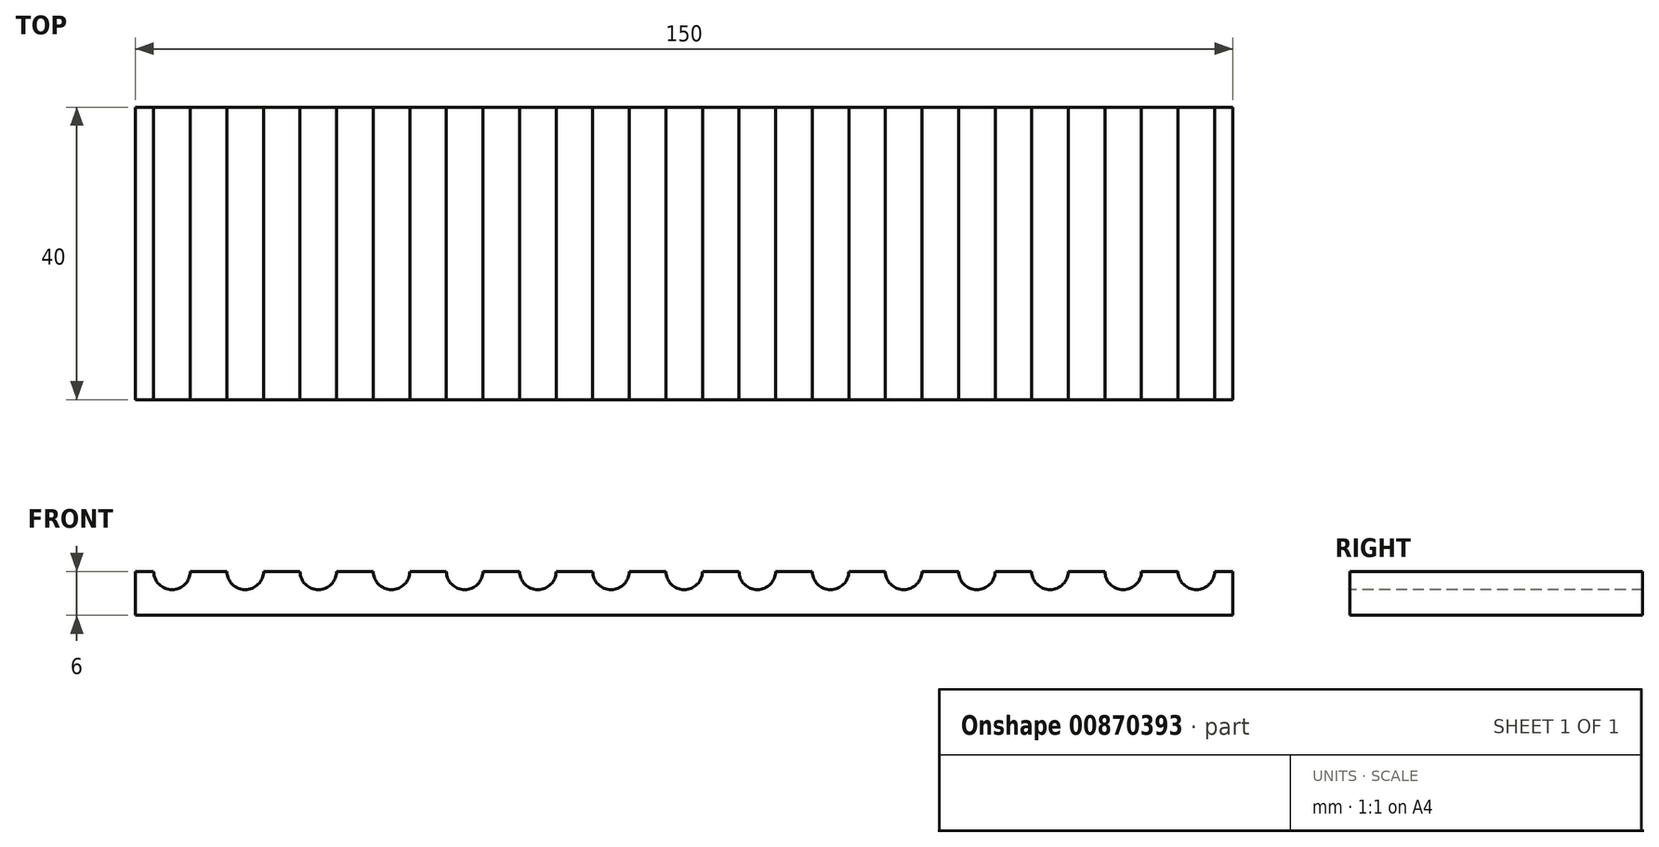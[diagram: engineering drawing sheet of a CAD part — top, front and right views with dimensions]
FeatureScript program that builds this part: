
annotation { "Feature Type Name" : "Feature", "Feature Type Description" : "" }
export const myFeature = defineFeature(function(context is Context, id is Id, definition is map)
    precondition{}
    {
        {
            var Q0;
            Q0=qCreatedBy(makeId("Front.planeOp"),FACE);
            var sketch = newSketch(context, id + "F0", { "sketchPlane" : qUnion([Q0])});
            skLineSegment(sketch, "E0.bottom", {"start": v(0, 0) * mm, "end": v(150, 0) * mm});
            skLineSegment(sketch, "E0.top", {"start": v(0, 6) * mm, "end": v(150, 6) * mm});
            skLineSegment(sketch, "E0.left", {"start": v(0, 0) * mm, "end": v(0, 6) * mm});
            skLineSegment(sketch, "E0.right", {"start": v(150, 0) * mm, "end": v(150, 6) * mm});
            skSolve(sketch);
        }
        {
            var Q0;
            Q0=makeQuery(id+"F0.imprint","IMPRINT",FACE,{"disambiguationData":[TD([[makeQuery(id+"F0.imprint","IMPRINT",EDGE,{"derivedFrom":sQuery(id+"F0.wireOp",EDGE,"E0.bottom")}),1.0]])]});
            extrude(context, id + "F1", {"entities" : qUnion([Q0]), "oppositeDirection" : true, "depth" : 40 * mm, "offsetDistance" : 25 * mm});
        }
        {
            var Q0;
            Q0=makeQuery(id+"F1.opExtrude","CAP_FACE",FACE,{"disambiguationData":[OSD([sQuery(id+"F0.wireOp",EDGE,"E0.bottom"),sQuery(id+"F0.wireOp",EDGE,"E0.top"),sQuery(id+"F0.wireOp",EDGE,"E0.left"),sQuery(id+"F0.wireOp",EDGE,"E0.right")])],"isStart":true});
            var sketch = newSketch(context, id + "F2", { "sketchPlane" : qUnion([Q0])});
            skCircle(sketch, "E1", {"center": v(5, 6) * mm, "radius": 2.5 * mm});
            skCircle(sketch, "E2.1.0.0", {"center": v(15, 6) * mm, "radius": 2.5 * mm});
            skCircle(sketch, "E2.2.0.0", {"center": v(25, 6) * mm, "radius": 2.5 * mm});
            skCircle(sketch, "E2.3.0.0", {"center": v(35, 6) * mm, "radius": 2.5 * mm});
            skCircle(sketch, "E2.4.0.0", {"center": v(45, 6) * mm, "radius": 2.5 * mm});
            skCircle(sketch, "E2.5.0.0", {"center": v(55, 6) * mm, "radius": 2.5 * mm});
            skCircle(sketch, "E2.6.0.0", {"center": v(65, 6) * mm, "radius": 2.5 * mm});
            skCircle(sketch, "E2.7.0.0", {"center": v(75, 6) * mm, "radius": 2.5 * mm});
            skCircle(sketch, "E2.8.0.0", {"center": v(85, 6) * mm, "radius": 2.5 * mm});
            skCircle(sketch, "E2.9.0.0", {"center": v(95, 6) * mm, "radius": 2.5 * mm});
            skCircle(sketch, "E2.10.0.0", {"center": v(105, 6) * mm, "radius": 2.5 * mm});
            skCircle(sketch, "E2.11.0.0", {"center": v(115, 6) * mm, "radius": 2.5 * mm});
            skCircle(sketch, "E2.12.0.0", {"center": v(125, 6) * mm, "radius": 2.5 * mm});
            skCircle(sketch, "E2.13.0.0", {"center": v(135, 6) * mm, "radius": 2.5 * mm});
            skCircle(sketch, "E2.14.0.0", {"center": v(145, 6) * mm, "radius": 2.5 * mm});
            skLineSegment(sketch, "E2.direction1", {"start": v(5, 6) * mm, "end": v(15, 6) * mm, "construction": true});
            skSolve(sketch);
        }
        {
            var Q0;
            {var subQ0=sQuery(id+"F2.wireOp",EDGE,"E1");var subQ1=makeQuery(id+"F1.opExtrude","CAP_EDGE",EDGE,{"disambiguationData":[OSD([sQuery(id+"F0.wireOp",EDGE,"E0.top")])],"isStart":true});var subQ2=makeQuery(id+"F2.imprint","INTERSECT",VERTEX,{"disambiguationData":[OD(0.0)],"derivedFrom":[subQ1,subQ0]});Q0=makeQuery(id+"F2.imprint","IMPRINT",FACE,{"disambiguationData":[TD([[makeQuery(id+"F2.imprint","IMPRINT",EDGE,{"disambiguationData":[TD([[subQ2,-1.0]])],"derivedFrom":subQ0}),1.0]])]});}
            var Q1;
            {var subQ0=sQuery(id+"F2.wireOp",EDGE,"E2.1.0.0");var subQ1=makeQuery(id+"F1.opExtrude","CAP_EDGE",EDGE,{"disambiguationData":[OSD([sQuery(id+"F0.wireOp",EDGE,"E0.top")])],"isStart":true});var subQ2=makeQuery(id+"F2.imprint","INTERSECT",VERTEX,{"disambiguationData":[OD(0.0)],"derivedFrom":[subQ1,subQ0]});Q1=makeQuery(id+"F2.imprint","IMPRINT",FACE,{"disambiguationData":[TD([[makeQuery(id+"F2.imprint","IMPRINT",EDGE,{"disambiguationData":[TD([[subQ2,-1.0]])],"derivedFrom":subQ0}),1.0]])]});}
            var Q2;
            {var subQ0=sQuery(id+"F2.wireOp",EDGE,"E2.2.0.0");var subQ1=makeQuery(id+"F1.opExtrude","CAP_EDGE",EDGE,{"disambiguationData":[OSD([sQuery(id+"F0.wireOp",EDGE,"E0.top")])],"isStart":true});var subQ2=makeQuery(id+"F2.imprint","INTERSECT",VERTEX,{"disambiguationData":[OD(0.0)],"derivedFrom":[subQ1,subQ0]});Q2=makeQuery(id+"F2.imprint","IMPRINT",FACE,{"disambiguationData":[TD([[makeQuery(id+"F2.imprint","IMPRINT",EDGE,{"disambiguationData":[TD([[subQ2,-1.0]])],"derivedFrom":subQ0}),1.0]])]});}
            var Q3;
            {var subQ0=sQuery(id+"F2.wireOp",EDGE,"E2.3.0.0");var subQ1=makeQuery(id+"F1.opExtrude","CAP_EDGE",EDGE,{"disambiguationData":[OSD([sQuery(id+"F0.wireOp",EDGE,"E0.top")])],"isStart":true});var subQ2=makeQuery(id+"F2.imprint","INTERSECT",VERTEX,{"disambiguationData":[OD(0.0)],"derivedFrom":[subQ1,subQ0]});Q3=makeQuery(id+"F2.imprint","IMPRINT",FACE,{"disambiguationData":[TD([[makeQuery(id+"F2.imprint","IMPRINT",EDGE,{"disambiguationData":[TD([[subQ2,-1.0]])],"derivedFrom":subQ0}),1.0]])]});}
            var Q4;
            {var subQ0=sQuery(id+"F2.wireOp",EDGE,"E2.4.0.0");var subQ1=makeQuery(id+"F1.opExtrude","CAP_EDGE",EDGE,{"disambiguationData":[OSD([sQuery(id+"F0.wireOp",EDGE,"E0.top")])],"isStart":true});var subQ2=makeQuery(id+"F2.imprint","INTERSECT",VERTEX,{"disambiguationData":[OD(0.0)],"derivedFrom":[subQ1,subQ0]});Q4=makeQuery(id+"F2.imprint","IMPRINT",FACE,{"disambiguationData":[TD([[makeQuery(id+"F2.imprint","IMPRINT",EDGE,{"disambiguationData":[TD([[subQ2,-1.0]])],"derivedFrom":subQ0}),1.0]])]});}
            var Q5;
            {var subQ0=sQuery(id+"F2.wireOp",EDGE,"E2.5.0.0");var subQ1=makeQuery(id+"F1.opExtrude","CAP_EDGE",EDGE,{"disambiguationData":[OSD([sQuery(id+"F0.wireOp",EDGE,"E0.top")])],"isStart":true});var subQ2=makeQuery(id+"F2.imprint","INTERSECT",VERTEX,{"disambiguationData":[OD(0.0)],"derivedFrom":[subQ1,subQ0]});Q5=makeQuery(id+"F2.imprint","IMPRINT",FACE,{"disambiguationData":[TD([[makeQuery(id+"F2.imprint","IMPRINT",EDGE,{"disambiguationData":[TD([[subQ2,-1.0]])],"derivedFrom":subQ0}),1.0]])]});}
            var Q6;
            {var subQ0=sQuery(id+"F2.wireOp",EDGE,"E2.6.0.0");var subQ1=makeQuery(id+"F1.opExtrude","CAP_EDGE",EDGE,{"disambiguationData":[OSD([sQuery(id+"F0.wireOp",EDGE,"E0.top")])],"isStart":true});var subQ2=makeQuery(id+"F2.imprint","INTERSECT",VERTEX,{"disambiguationData":[OD(0.0)],"derivedFrom":[subQ1,subQ0]});Q6=makeQuery(id+"F2.imprint","IMPRINT",FACE,{"disambiguationData":[TD([[makeQuery(id+"F2.imprint","IMPRINT",EDGE,{"disambiguationData":[TD([[subQ2,-1.0]])],"derivedFrom":subQ0}),1.0]])]});}
            var Q7;
            {var subQ0=sQuery(id+"F2.wireOp",EDGE,"E2.7.0.0");var subQ1=makeQuery(id+"F1.opExtrude","CAP_EDGE",EDGE,{"disambiguationData":[OSD([sQuery(id+"F0.wireOp",EDGE,"E0.top")])],"isStart":true});var subQ2=makeQuery(id+"F2.imprint","INTERSECT",VERTEX,{"disambiguationData":[OD(0.0)],"derivedFrom":[subQ1,subQ0]});Q7=makeQuery(id+"F2.imprint","IMPRINT",FACE,{"disambiguationData":[TD([[makeQuery(id+"F2.imprint","IMPRINT",EDGE,{"disambiguationData":[TD([[subQ2,-1.0]])],"derivedFrom":subQ0}),1.0]])]});}
            var Q8;
            {var subQ0=sQuery(id+"F2.wireOp",EDGE,"E2.8.0.0");var subQ1=makeQuery(id+"F1.opExtrude","CAP_EDGE",EDGE,{"disambiguationData":[OSD([sQuery(id+"F0.wireOp",EDGE,"E0.top")])],"isStart":true});var subQ2=makeQuery(id+"F2.imprint","INTERSECT",VERTEX,{"disambiguationData":[OD(0.0)],"derivedFrom":[subQ1,subQ0]});Q8=makeQuery(id+"F2.imprint","IMPRINT",FACE,{"disambiguationData":[TD([[makeQuery(id+"F2.imprint","IMPRINT",EDGE,{"disambiguationData":[TD([[subQ2,1.0]])],"derivedFrom":subQ0}),1.0]])]});}
            var Q9;
            {var subQ0=sQuery(id+"F2.wireOp",EDGE,"E2.9.0.0");var subQ1=makeQuery(id+"F1.opExtrude","CAP_EDGE",EDGE,{"disambiguationData":[OSD([sQuery(id+"F0.wireOp",EDGE,"E0.top")])],"isStart":true});var subQ2=makeQuery(id+"F2.imprint","INTERSECT",VERTEX,{"disambiguationData":[OD(0.0)],"derivedFrom":[subQ1,subQ0]});Q9=makeQuery(id+"F2.imprint","IMPRINT",FACE,{"disambiguationData":[TD([[makeQuery(id+"F2.imprint","IMPRINT",EDGE,{"disambiguationData":[TD([[subQ2,1.0]])],"derivedFrom":subQ0}),1.0]])]});}
            var Q10;
            {var subQ0=sQuery(id+"F2.wireOp",EDGE,"E2.10.0.0");var subQ1=makeQuery(id+"F1.opExtrude","CAP_EDGE",EDGE,{"disambiguationData":[OSD([sQuery(id+"F0.wireOp",EDGE,"E0.top")])],"isStart":true});var subQ2=makeQuery(id+"F2.imprint","INTERSECT",VERTEX,{"disambiguationData":[OD(0.0)],"derivedFrom":[subQ1,subQ0]});Q10=makeQuery(id+"F2.imprint","IMPRINT",FACE,{"disambiguationData":[TD([[makeQuery(id+"F2.imprint","IMPRINT",EDGE,{"disambiguationData":[TD([[subQ2,1.0]])],"derivedFrom":subQ0}),1.0]])]});}
            var Q11;
            {var subQ0=sQuery(id+"F2.wireOp",EDGE,"E2.11.0.0");var subQ1=makeQuery(id+"F1.opExtrude","CAP_EDGE",EDGE,{"disambiguationData":[OSD([sQuery(id+"F0.wireOp",EDGE,"E0.top")])],"isStart":true});var subQ2=makeQuery(id+"F2.imprint","INTERSECT",VERTEX,{"disambiguationData":[OD(0.0)],"derivedFrom":[subQ1,subQ0]});Q11=makeQuery(id+"F2.imprint","IMPRINT",FACE,{"disambiguationData":[TD([[makeQuery(id+"F2.imprint","IMPRINT",EDGE,{"disambiguationData":[TD([[subQ2,1.0]])],"derivedFrom":subQ0}),1.0]])]});}
            var Q12;
            {var subQ0=sQuery(id+"F2.wireOp",EDGE,"E2.12.0.0");var subQ1=makeQuery(id+"F1.opExtrude","CAP_EDGE",EDGE,{"disambiguationData":[OSD([sQuery(id+"F0.wireOp",EDGE,"E0.top")])],"isStart":true});var subQ2=makeQuery(id+"F2.imprint","INTERSECT",VERTEX,{"disambiguationData":[OD(0.0)],"derivedFrom":[subQ1,subQ0]});Q12=makeQuery(id+"F2.imprint","IMPRINT",FACE,{"disambiguationData":[TD([[makeQuery(id+"F2.imprint","IMPRINT",EDGE,{"disambiguationData":[TD([[subQ2,1.0]])],"derivedFrom":subQ0}),1.0]])]});}
            var Q13;
            {var subQ0=sQuery(id+"F2.wireOp",EDGE,"E2.13.0.0");var subQ1=makeQuery(id+"F1.opExtrude","CAP_EDGE",EDGE,{"disambiguationData":[OSD([sQuery(id+"F0.wireOp",EDGE,"E0.top")])],"isStart":true});var subQ2=makeQuery(id+"F2.imprint","INTERSECT",VERTEX,{"disambiguationData":[OD(0.0)],"derivedFrom":[subQ1,subQ0]});Q13=makeQuery(id+"F2.imprint","IMPRINT",FACE,{"disambiguationData":[TD([[makeQuery(id+"F2.imprint","IMPRINT",EDGE,{"disambiguationData":[TD([[subQ2,1.0]])],"derivedFrom":subQ0}),1.0]])]});}
            var Q14;
            {var subQ0=sQuery(id+"F2.wireOp",EDGE,"E2.14.0.0");var subQ1=makeQuery(id+"F1.opExtrude","CAP_EDGE",EDGE,{"disambiguationData":[OSD([sQuery(id+"F0.wireOp",EDGE,"E0.top")])],"isStart":true});var subQ2=makeQuery(id+"F2.imprint","INTERSECT",VERTEX,{"disambiguationData":[OD(0.0)],"derivedFrom":[subQ1,subQ0]});Q14=makeQuery(id+"F2.imprint","IMPRINT",FACE,{"disambiguationData":[TD([[makeQuery(id+"F2.imprint","IMPRINT",EDGE,{"disambiguationData":[TD([[subQ2,1.0]])],"derivedFrom":subQ0}),1.0]])]});}
            extrude(context, id + "F3", {"entities" : qUnion([Q0, Q1, Q2, Q3, Q4, Q5, Q6, Q7, Q8, Q9, Q10, Q11, Q12, Q13, Q14]), "operationType" : NewBodyOperationType.REMOVE, "endBound" : BoundingType.THROUGH_ALL, "oppositeDirection" : true, "depth" : 25 * mm, "offsetDistance" : 25 * mm});
        }
    });
